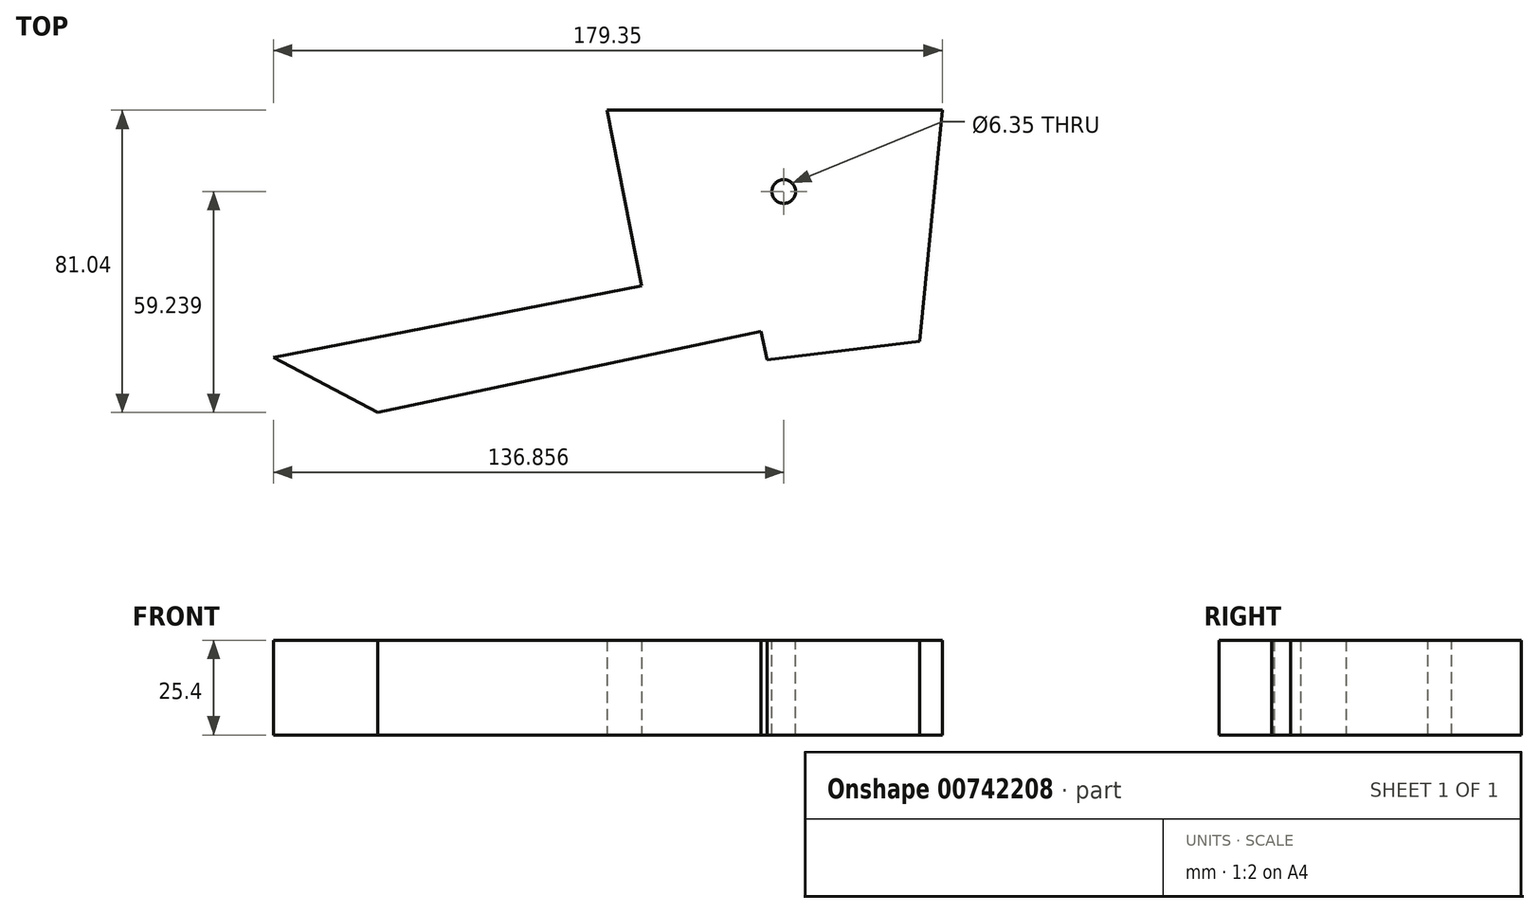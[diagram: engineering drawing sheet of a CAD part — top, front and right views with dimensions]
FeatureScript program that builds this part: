
annotation { "Feature Type Name" : "Feature", "Feature Type Description" : "" }
export const myFeature = defineFeature(function(context is Context, id is Id, definition is map)
    precondition{}
    {
        {
            var Q0;
            Q0=qCreatedBy(makeId("Top.planeOp"),FACE);
            var sketch = newSketch(context, id + "F0", { "sketchPlane" : qUnion([Q0])});
            skLineSegment(sketch, "E0", {"start": v(-116.03, -49.22) * mm, "end": v(-13.2, -27.43) * mm});
            skLineSegment(sketch, "E1", {"start": v(-13.2, -27.43) * mm, "end": v(-11.58, -35.08) * mm});
            skLineSegment(sketch, "E2", {"start": v(-11.58, -35.08) * mm, "end": v(29.23, -30.1) * mm});
            skLineSegment(sketch, "E3", {"start": v(29.23, -30.1) * mm, "end": v(35.35, 31.82) * mm});
            skLineSegment(sketch, "E4", {"start": v(35.35, 31.82) * mm, "end": v(-54.49, 31.82) * mm});
            skLineSegment(sketch, "E5", {"start": v(-54.49, 31.82) * mm, "end": v(-45.31, -15.2) * mm});
            skLineSegment(sketch, "E6", {"start": v(-45.31, -15.2) * mm, "end": v(-144, -34.45) * mm});
            skLineSegment(sketch, "E7", {"start": v(-144, -34.45) * mm, "end": v(-116.03, -49.22) * mm});
            skSolve(sketch);
        }
        {
            var Q0;
            Q0 = qSketchRegion(id + "F0", true);
            extrude(context, id + "F1", {"entities" : qUnion([Q0]), "endBound" : BoundingType.SYMMETRIC, "depth" : 25.4 * mm, "offsetDistance" : 25.4 * mm});
        }
        {
            var Q0;
            Q0=makeQuery(id+"F1.opExtrude","CAP_FACE",FACE,{"disambiguationData":[OSD([sQuery(id+"F0.wireOp",EDGE,"E0"),sQuery(id+"F0.wireOp",EDGE,"E1"),sQuery(id+"F0.wireOp",EDGE,"E2"),sQuery(id+"F0.wireOp",EDGE,"E3"),sQuery(id+"F0.wireOp",EDGE,"E4"),sQuery(id+"F0.wireOp",EDGE,"E5"),sQuery(id+"F0.wireOp",EDGE,"E6"),sQuery(id+"F0.wireOp",EDGE,"E7")])],"isStart":false});
            var sketch = newSketch(context, id + "F2", { "sketchPlane" : qUnion([Q0])});
            skCircle(sketch, "E8", {"center": v(-7.14, 10.02) * mm, "radius": 6.35 * mm});
            skSolve(sketch);
        }
        {
            var Q0;
            Q0=sQuery(id+"F2.wireOp",VERTEX,"E8.center");
            var Q1;
            Q1=makeQuery(id+"F1.opExtrude","SWEPT_BODY",BODY,{"disambiguationData":[OSD([sQuery(id+"F0.wireOp",EDGE,"E0"),sQuery(id+"F0.wireOp",EDGE,"E1"),sQuery(id+"F0.wireOp",EDGE,"E2"),sQuery(id+"F0.wireOp",EDGE,"E3"),sQuery(id+"F0.wireOp",EDGE,"E4"),sQuery(id+"F0.wireOp",EDGE,"E5"),sQuery(id+"F0.wireOp",EDGE,"E6"),sQuery(id+"F0.wireOp",EDGE,"E7")])]});
            hole(context, id + "F3", {"style" : HoleStyle.SIMPLE, "endStyle" : HoleEndStyle.THROUGH, "holeDiameter" : 6.35 * mm, "majorDiameter" : 6.35 * mm, "isTappedThrough" : true, "tappedDepth" : 12.7 * mm, "tapClearance" : 3, "locations" : qUnion([Q0]), "scope" : qUnion([Q1])});
        }
    });
